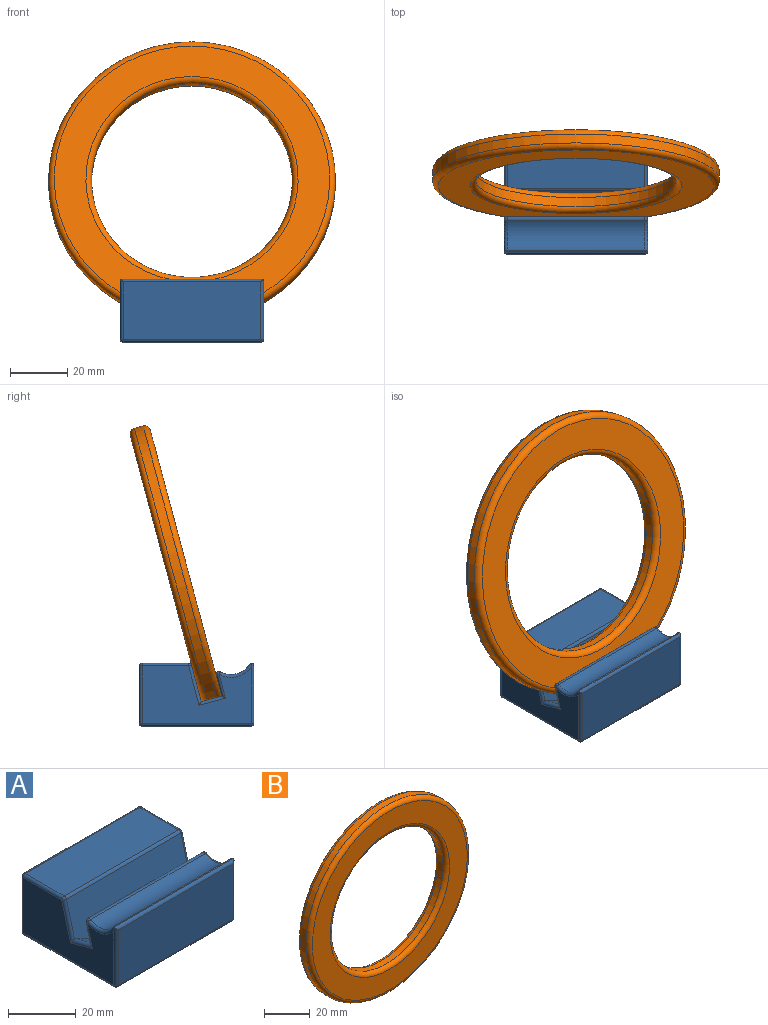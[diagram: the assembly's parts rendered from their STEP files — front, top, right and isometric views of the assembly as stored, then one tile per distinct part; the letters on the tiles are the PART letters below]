
ASSEMBLY  parts=2 mates=1
PART A: 43 faces, bbox 50x41x22.2 mm
  f0: plane 38x20mm, normal (1,0,0), area 600.8mm2, adj f12,f13,f14,f15,f16,f17,f18,f19
  f1: plane 48x16.23mm, normal (0,0,1), area 779.2mm2, adj f12,f22,f31,f41
  f2: plane 48x38mm, normal (0,0,-1), area 1824mm2, adj f15,f23,f35,f38
  f3: plane 49.48x0.37mm, normal (0,0,1), area 18mm2, adj f10,f19,f27,f33
  f4: plane 38x20mm, normal (-1,0,0), area 600.8mm2, adj f21,f22,f23,f24,f25,f26,f27,f28
  f5: plane 48x20mm, normal (0,-1,0), area 960mm2, adj f17,f25,f33,f35
  f6: plane 48x20mm, normal (0,1,0), area 960mm2, adj f13,f21,f31,f38
  f7: plane 48x18.51mm, normal (0,-0.97,0.26), area 824.3mm2, adj f9,f14,f16,f24,f26,f41
  f8: plane 48x13.13mm, normal (0,0.97,-0.26), area 557.1mm2, adj f9,f11,f16,f18,f26,f28
  f9: cylinder r=50.15mm len=47.06mm, axis (0,0.97,-0.26), area 367.4mm2, adj f7,f8,f16,f26
  f10: cylinder r=7.5mm len=48mm, axis (1,0,0), area 574.3mm2, adj f3,f11,f19,f27
  f11: cylinder r=1mm len=48mm, axis (1,0,0), area 112.5mm2, adj f8,f10,f20,f29
  f12: cylinder r=1mm len=16.23mm, axis (0,1,0), area 25.5mm2, adj f0,f1,f32,f40
  f13: cylinder r=1mm len=20mm, axis (0,0,1), area 31.4mm2, adj f0,f6,f32,f39
  f14: cylinder r=1mm len=13.95mm, axis (0,0.26,0.97), area 21.3mm2, adj f0,f7,f16,f40
  f15: cylinder r=1mm len=38mm, axis (0,-1,0), area 59.7mm2, adj f0,f2,f36,f39
  f16: cylinder r=1mm len=9.44mm, axis (0,0.97,-0.26), area 16.6mm2, adj f0,f7,f8,f9,f14,f18
  f17: cylinder r=1mm len=20.94mm, axis (0,0,-1), area 32.2mm2, adj f0,f5,f19,f33,f36
  f18: cylinder r=1mm len=8.58mm, axis (0,-0.26,-0.97), area 12.5mm2, adj f0,f8,f16,f20
  f19: torus R=8.5mm, axis (-1,0,0), area 19.7mm2, adj f0,f3,f10,f17,f20,f33
  f20: sphere r=1mm, area 2.3mm2, adj f11,f18,f19
  f21: cylinder r=1mm len=20mm, axis (0,0,-1), area 31.4mm2, adj f4,f6,f30,f37
  f22: cylinder r=1mm len=16.23mm, axis (0,-1,0), area 25.5mm2, adj f1,f4,f30,f42
  f23: cylinder r=1mm len=38mm, axis (0,1,0), area 59.7mm2, adj f2,f4,f34,f37
  f24: cylinder r=1mm len=13.95mm, axis (0,0.26,0.97), area 21.3mm2, adj f4,f7,f26,f42
  f25: cylinder r=1mm len=20.94mm, axis (0,0,1), area 32.2mm2, adj f4,f5,f27,f33,f34
  f26: cylinder r=1mm len=9.44mm, axis (0,0.97,-0.26), area 16.6mm2, adj f4,f7,f8,f9,f24,f28
  f27: torus R=8.5mm, axis (-1,0,0), area 19.7mm2, adj f3,f4,f10,f25,f29,f33
  f28: cylinder r=1mm len=8.58mm, axis (0,0.26,0.97), area 12.5mm2, adj f4,f8,f26,f29
  f29: sphere r=1mm, area 2.3mm2, adj f11,f27,f28
  f30: sphere r=1mm, area 1.6mm2, adj f21,f22,f31
  f31: cylinder r=1mm len=48mm, axis (-1,0,0), area 75.4mm2, adj f1,f6,f30,f32
  f32: sphere r=1mm, area 1.6mm2, adj f12,f13,f31
  f33: cylinder r=1mm len=49.88mm, axis (1,0,0), area 77.3mm2, adj f3,f5,f17,f19,f25,f27
  f34: sphere r=1mm, area 1.6mm2, adj f23,f25,f35
  f35: cylinder r=1mm len=48mm, axis (-1,0,0), area 75.4mm2, adj f2,f5,f34,f36
  f36: sphere r=1mm, area 1.6mm2, adj f15,f17,f35
  f37: sphere r=1mm, area 1.6mm2, adj f21,f23,f38
  f38: cylinder r=1mm len=48mm, axis (1,0,0), area 75.4mm2, adj f2,f6,f37,f39
  f39: sphere r=1mm, area 1.6mm2, adj f13,f15,f38
  f40: sphere r=1mm, area 1.3mm2, adj f12,f14,f41
  f41: cylinder r=1mm len=48mm, axis (-1,0,0), area 62.8mm2, adj f1,f7,f40,f42
  f42: sphere r=1mm, area 1.3mm2, adj f22,f24,f41
PART B: 8 faces, bbox 108.2x7.2x108.2 mm
  f0: cylinder r=35mm len=70mm, axis (0,1,0), area 703.7mm2, adj f4,f6
  f1: cylinder r=50mm len=100mm, axis (0,1,0), area 1005.3mm2, adj f5,f7
  f2: plane 96x96mm, normal (0,-1,0), area 2937.4mm2, adj f6,f7
  f3: plane 96x96mm, normal (0,1,0), area 2937.4mm2, adj f4,f5
  f4: torus R=37mm, axis (0,-1,0), area 705.2mm2, adj f0,f3
  f5: torus R=48mm, axis (0,-1,0), area 972.6mm2, adj f1,f3
  f6: torus R=37mm, axis (0,-1,0), area 705.2mm2, adj f0,f2
  f7: torus R=48mm, axis (0,-1,0), area 972.6mm2, adj f1,f2
PLACE A t=(-18.23,11.98,-9.73)mm
PLACE B rot(axis=(1,0,0),165deg) t=(-18.23,-4.3,36.11)mm
MATE planar B.f1 <-> A.f9  axis (0,-0.97,0.26) through (-18.23,-0.82,35.18)mm
